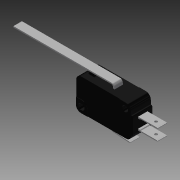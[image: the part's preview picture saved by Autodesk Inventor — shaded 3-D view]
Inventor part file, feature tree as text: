
AUTODESK INVENTOR PART (.ipt)
format: ipt  version: 2018 (Build 220112000, 112)  size: 358,400 bytes
history: native  units: in
note: dims shown in document units (in); Inventor stores cm internally (conversion verified against a paired STEP export)
features: extrude x6, sketch x2, hole x2
ambient origin geometry x8: Origin, YZ Plane, XZ Plane, XY Plane, X Axis, Y Axis, Z Axis, Center Point
bodies: Solid1 (feature_tree)
feature tree (10):
  sketch  "Sketch1"  dims[d0=0.8749in d1=0.8749in d2=1.135in d3=1.135in]
  extrude  "Extrusion1"  Depth=1.135in
  sketch  "Sketch2"  dims[d4=0.4054in d5=0.4054in d6=0.17in d7=0.0in d8=0.3854in d9=0.3854in d10=0.6024in d11=0.6024in d12=0.402in d13=0.402in d14=0.24in d15=0.24in d16=0.6529in d17=0.6529in d18=2.3471in d19=2.3471in d20=0.02in d21=0.02in d22=0.125in d23=0.125in d24=0.187in d25=0.187in d26=0.126in d27=0.126in d28=0.235in d29=0.235in d30=0.0104in d31=0.0104in d32=0.54in d33=0.54in d34=0.323in d35=0.323in d36=0.114in d37=0.114in d38=0.11in d39=0.11in d40=0.116in d41=0.116in d42=0.626in d43=0.626in d44=0.04in d45=0.04in d46=0.386in d47=0.0in d48=0.402in d49=0.0in d50=0.402in d51=0.0in d52=0.15in d53=0.0in d54=0.17in d55=0.0in d56=0.187in d57=0.0in d58=0.125in d59=0.0935in d60=0.055in d61=0.5in d62=0.375in d63=0.25in d64=0.5635in d65=0.75in d66=0.8108in d67=0.0935in d68=0.125in d69=0.055in d70=0.5in d71=0.375in d72=0.25in d73=0.5635in d74=0.75in d75=0.8108in]
  extrude  "Extrusion2"  Depth=0.17in TaperAngle=0.0deg
  extrude  "Extrusion3"  Depth=0.187in
  extrude  "Extrusion4"  Depth=0.187in
  extrude  "Extrusion5"  Depth=0.402in
  extrude  "Extrusion6"  Depth=0.24in
  hole  "Hole1"  [1 undecoded]
  hole  "Hole2"  [1 undecoded]
note: 2 required parameter values undecoded (feature->parameter linkage not recoverable at this tier; creation-order binding heuristic only, values carry confidence <= 0.55)
